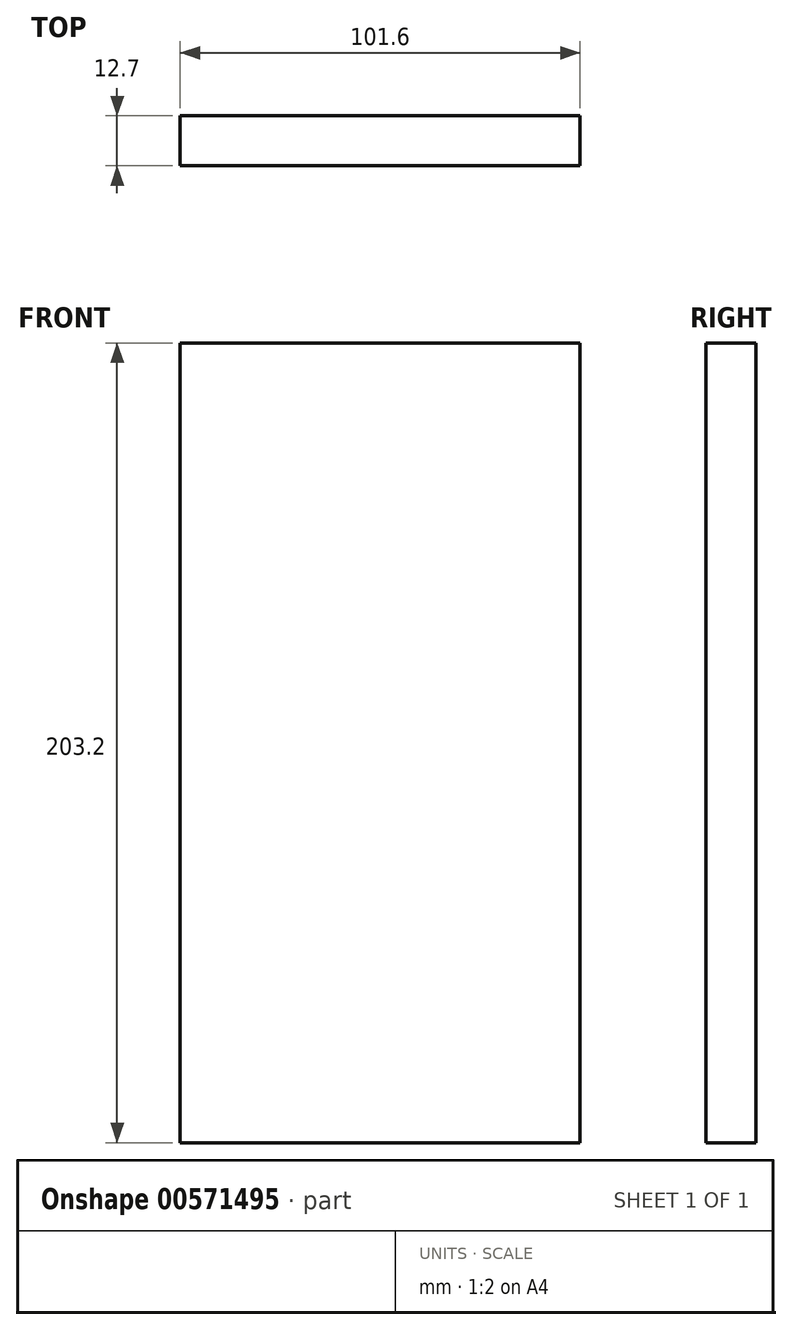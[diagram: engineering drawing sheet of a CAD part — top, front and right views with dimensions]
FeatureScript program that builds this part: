
annotation { "Feature Type Name" : "Feature", "Feature Type Description" : "" }
export const myFeature = defineFeature(function(context is Context, id is Id, definition is map)
    precondition{}
    {
        {
            var Q0;
            Q0=qCreatedBy(makeId("Front.planeOp"),FACE);
            var sketch = newSketch(context, id + "F0", { "sketchPlane" : qUnion([Q0])});
            skLineSegment(sketch, "E0", {"start": v(-58.97, 176.68) * mm, "end": v(-58.97, -26.52) * mm});
            skLineSegment(sketch, "E1", {"start": v(-58.97, -26.52) * mm, "end": v(42.63, -26.52) * mm});
            skLineSegment(sketch, "E2", {"start": v(42.63, -26.52) * mm, "end": v(42.63, 176.68) * mm});
            skLineSegment(sketch, "E3", {"start": v(42.63, 176.68) * mm, "end": v(-58.97, 176.68) * mm});
            skSolve(sketch);
        }
        {
            var Q0;
            Q0 = qSketchRegion(id + "F0", true);
            extrude(context, id + "F1", {"entities" : qUnion([Q0]), "depth" : 12.7 * mm, "offsetDistance" : 25.4 * mm});
        }
    });
